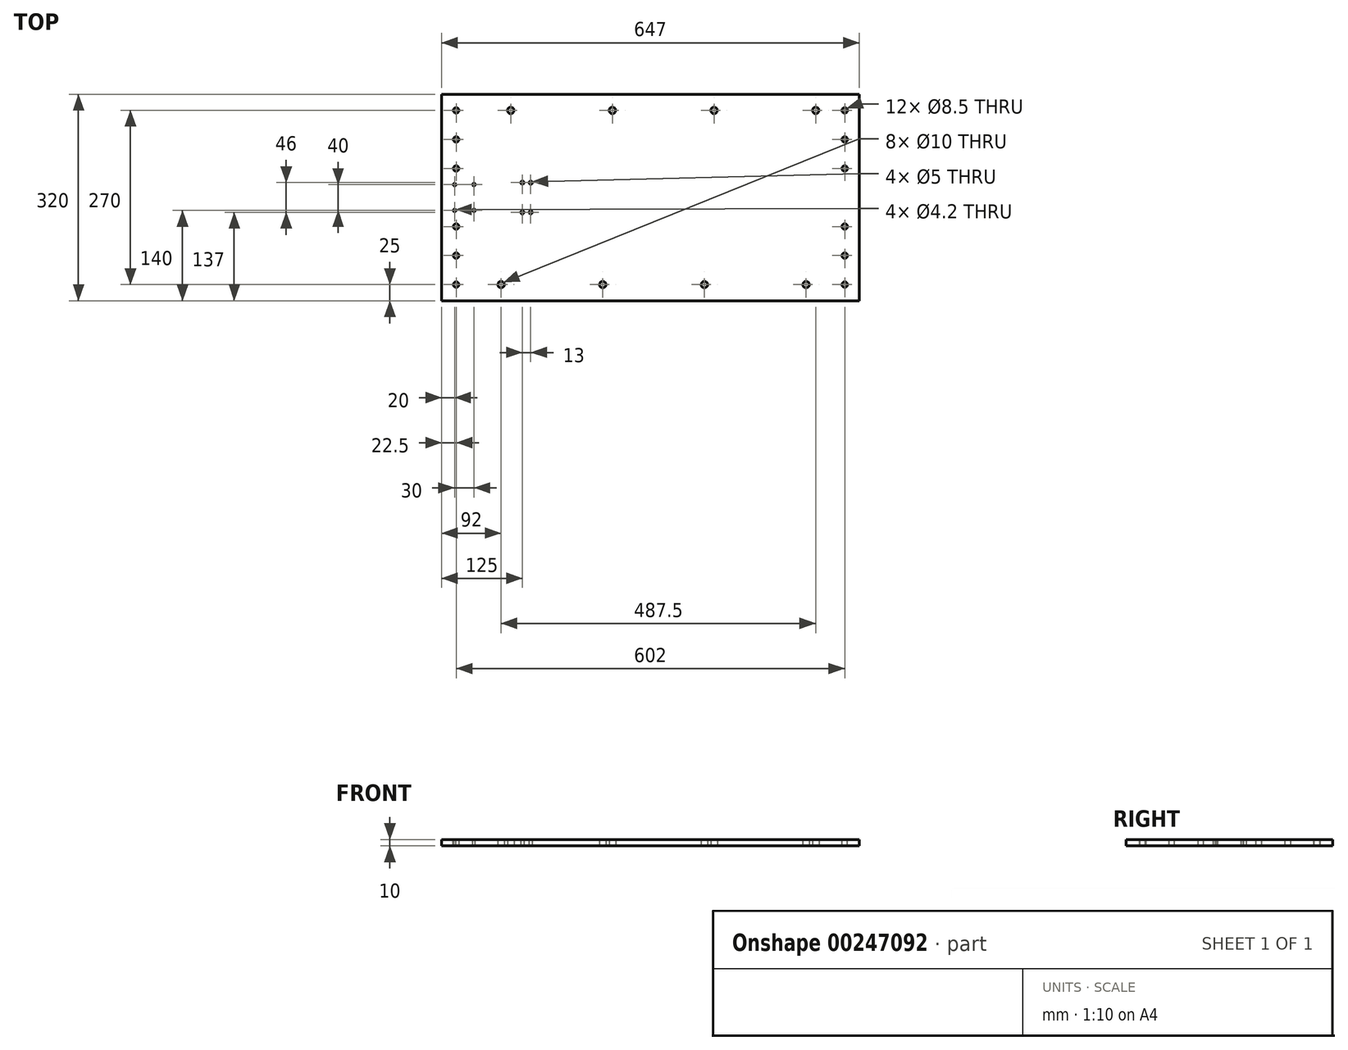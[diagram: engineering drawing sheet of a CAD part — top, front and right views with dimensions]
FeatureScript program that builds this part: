
annotation { "Feature Type Name" : "Feature", "Feature Type Description" : "" }
export const myFeature = defineFeature(function(context is Context, id is Id, definition is map)
    precondition{}
    {
        {
            var Q0;
            Q0=qCreatedBy(makeId("Top.planeOp"),FACE);
            var sketch = newSketch(context, id + "F0", { "sketchPlane" : qUnion([Q0])});
            skLineSegment(sketch, "E0.bottom", {"start": v(0, 0) * mm, "end": v(647, 0) * mm});
            skLineSegment(sketch, "E0.top", {"start": v(0, 320) * mm, "end": v(647, 320) * mm});
            skLineSegment(sketch, "E0.left", {"start": v(0, 0) * mm, "end": v(0, 320) * mm});
            skLineSegment(sketch, "E0.right", {"start": v(647, 0) * mm, "end": v(647, 320) * mm});
            skLineSegment(sketch, "E1", {"start": v(-62.37, 160) * mm, "end": v(1061.73, 160) * mm, "construction": true});
            skPoint(sketch, "E1.startSnap0", {"position": v(0, 160) * mm});
            skPoint(sketch, "E2", {"position": v(92, 25) * mm});
            skPoint(sketch, "E3.1.0.0", {"position": v(144.5, 25) * mm});
            skPoint(sketch, "E3.2.0.0", {"position": v(197, 25) * mm});
            skPoint(sketch, "E3.3.0.0", {"position": v(249.5, 25) * mm});
            skPoint(sketch, "E3.4.0.0", {"position": v(302, 25) * mm});
            skPoint(sketch, "E3.5.0.0", {"position": v(354.5, 25) * mm});
            skPoint(sketch, "E3.6.0.0", {"position": v(407, 25) * mm});
            skPoint(sketch, "E3.7.0.0", {"position": v(459.5, 25) * mm});
            skPoint(sketch, "E3.8.0.0", {"position": v(512, 25) * mm});
            skLineSegment(sketch, "E3.direction1", {"start": v(92, 25) * mm, "end": v(144.5, 25) * mm, "construction": true});
            skPoint(sketch, "E4", {"position": v(107, 295) * mm});
            skPoint(sketch, "E5.1.0.0", {"position": v(159.5, 295) * mm});
            skPoint(sketch, "E5.2.0.0", {"position": v(212, 295) * mm});
            skPoint(sketch, "E5.3.0.0", {"position": v(264.5, 295) * mm});
            skPoint(sketch, "E5.4.0.0", {"position": v(317, 295) * mm});
            skPoint(sketch, "E5.5.0.0", {"position": v(369.5, 295) * mm});
            skPoint(sketch, "E5.6.0.0", {"position": v(422, 295) * mm});
            skPoint(sketch, "E5.7.0.0", {"position": v(474.5, 295) * mm});
            skLineSegment(sketch, "E5.direction1", {"start": v(107, 295) * mm, "end": v(159.5, 295) * mm, "construction": true});
            skPoint(sketch, "E6.0.8.0", {"position": v(527, 295) * mm});
            skPoint(sketch, "E7.0.9.0", {"position": v(579.5, 295) * mm});
            skPoint(sketch, "E8.0.9.0", {"position": v(564.5, 25) * mm});
            skPoint(sketch, "E9", {"position": v(125, 183) * mm});
            skPoint(sketch, "E10.0.1.0", {"position": v(125, 137) * mm});
            skPoint(sketch, "E10.1.0.0", {"position": v(138, 183) * mm});
            skPoint(sketch, "E10.1.1.0", {"position": v(138, 137) * mm});
            skLineSegment(sketch, "E10.direction1", {"start": v(125, 183) * mm, "end": v(138, 183) * mm, "construction": true});
            skLineSegment(sketch, "E10.direction2", {"start": v(125, 183) * mm, "end": v(125, 137) * mm, "construction": true});
            skLineSegment(sketch, "E11", {"start": v(22.5, 340.04) * mm, "end": v(22.5, -24.03) * mm, "construction": true});
            skPoint(sketch, "E12", {"position": v(22.5, 160) * mm});
            skPoint(sketch, "E13.0.1.0", {"position": v(22.5, 205) * mm});
            skPoint(sketch, "E13.0.2.0", {"position": v(22.5, 250) * mm});
            skLineSegment(sketch, "E13.direction1", {"start": v(22.5, 160) * mm, "end": v(47.5, 160) * mm, "construction": true});
            skLineSegment(sketch, "E13.direction2", {"start": v(22.5, 160) * mm, "end": v(22.5, 205) * mm, "construction": true});
            skPoint(sketch, "E14.0.1.0", {"position": v(22.5, 115) * mm});
            skPoint(sketch, "E14.0.2.0", {"position": v(22.5, 70) * mm});
            skLineSegment(sketch, "E14.direction2", {"start": v(22.5, 160) * mm, "end": v(22.5, 115) * mm, "construction": true});
            skPoint(sketch, "E15.0.0.3", {"position": v(22.5, 25) * mm});
            skPoint(sketch, "E16.0.0.3", {"position": v(22.5, 295) * mm});
            skSolve(sketch);
        }
        {
            var Q0;
            Q0=makeQuery(id+"F0.imprint","IMPRINT",FACE,{"disambiguationData":[TD([[makeQuery(id+"F0.imprint","IMPRINT",EDGE,{"derivedFrom":sQuery(id+"F0.wireOp",EDGE,"E0.bottom")}),1.0]])]});
            extrude(context, id + "F1", {"entities" : qUnion([Q0]), "depth" : 10 * mm, "offsetDistance" : 25 * mm});
        }
        {
            var Q0;
            Q0=sQuery(id+"F0.wireOp",VERTEX,"E2");
            var Q1;
            Q1=sQuery(id+"F0.wireOp",VERTEX,"E3.3.0.0");
            var Q2;
            Q2=sQuery(id+"F0.wireOp",VERTEX,"E3.6.0.0");
            var Q3;
            Q3=sQuery(id+"F0.wireOp",VERTEX,"E8.0.9.0");
            var Q4;
            Q4=sQuery(id+"F0.wireOp",VERTEX,"E4");
            var Q5;
            Q5=sQuery(id+"F0.wireOp",VERTEX,"E5.3.0.0");
            var Q6;
            Q6=sQuery(id+"F0.wireOp",VERTEX,"E5.6.0.0");
            var Q7;
            Q7=sQuery(id+"F0.wireOp",VERTEX,"E7.0.9.0");
            var Q8;
            Q8=makeQuery(id+"F1.opExtrude","SWEPT_BODY",BODY,{"disambiguationData":[OSD([sQuery(id+"F0.wireOp",EDGE,"E0.bottom"),sQuery(id+"F0.wireOp",EDGE,"E0.top"),sQuery(id+"F0.wireOp",EDGE,"E0.left"),sQuery(id+"F0.wireOp",EDGE,"E0.right")])]});
            hole(context, id + "F2", {"style" : HoleStyle.SIMPLE, "endStyle" : HoleEndStyle.THROUGH, "oppositeDirection" : true, "holeDiameter" : 10 * mm, "majorDiameter" : 5 * mm, "isTappedThrough" : true, "tappedDepth" : 12 * mm, "tapClearance" : 3, "locations" : qUnion([Q0, Q1, Q2, Q3, Q4, Q5, Q6, Q7]), "scope" : qUnion([Q8])});
        }
        {
            var Q0;
            Q0=sQuery(id+"F0.wireOp",VERTEX,"E10.1.0.0");
            var Q1;
            Q1=sQuery(id+"F0.wireOp",VERTEX,"E9");
            var Q2;
            Q2=sQuery(id+"F0.wireOp",VERTEX,"E10.0.1.0");
            var Q3;
            Q3=sQuery(id+"F0.wireOp",VERTEX,"E10.1.1.0");
            var Q4;
            Q4=makeQuery(id+"F1.opExtrude","SWEPT_BODY",BODY,{"disambiguationData":[OSD([sQuery(id+"F0.wireOp",EDGE,"E0.bottom"),sQuery(id+"F0.wireOp",EDGE,"E0.top"),sQuery(id+"F0.wireOp",EDGE,"E0.left"),sQuery(id+"F0.wireOp",EDGE,"E0.right")])]});
            hole(context, id + "F3", {"style" : HoleStyle.SIMPLE, "endStyle" : HoleEndStyle.THROUGH, "oppositeDirection" : true, "holeDiameter" : 5 * mm, "majorDiameter" : 5 * mm, "isTappedThrough" : true, "tappedDepth" : 12 * mm, "tapClearance" : 3, "locations" : qUnion([Q0, Q1, Q2, Q3]), "scope" : qUnion([Q4])});
        }
        {
            var Q0;
            Q0=sQuery(id+"F0.wireOp",VERTEX,"E13.0.2.0");
            var Q1;
            Q1=sQuery(id+"F0.wireOp",VERTEX,"E13.0.1.0");
            var Q2;
            Q2=sQuery(id+"F0.wireOp",VERTEX,"E14.0.1.0");
            var Q3;
            Q3=sQuery(id+"F0.wireOp",VERTEX,"E14.0.2.0");
            var Q4;
            Q4=sQuery(id+"F0.wireOp",VERTEX,"E16.0.0.3");
            var Q5;
            Q5=sQuery(id+"F0.wireOp",VERTEX,"E15.0.0.3");
            var Q6;
            Q6=makeQuery(id+"F1.opExtrude","SWEPT_BODY",BODY,{"disambiguationData":[OSD([sQuery(id+"F0.wireOp",EDGE,"E0.bottom"),sQuery(id+"F0.wireOp",EDGE,"E0.top"),sQuery(id+"F0.wireOp",EDGE,"E0.left"),sQuery(id+"F0.wireOp",EDGE,"E0.right")])]});
            hole(context, id + "F4", {"style" : HoleStyle.SIMPLE, "endStyle" : HoleEndStyle.THROUGH, "oppositeDirection" : true, "holeDiameter" : 8.5 * mm, "majorDiameter" : 5 * mm, "isTappedThrough" : true, "tappedDepth" : 12 * mm, "tapClearance" : 3, "locations" : qUnion([Q0, Q1, Q2, Q3, Q4, Q5]), "scope" : qUnion([Q6])});
        }
        {
            var Q0;
            Q0=makeQuery(id+"F1.opExtrude","CAP_FACE",FACE,{"disambiguationData":[OSD([sQuery(id+"F0.wireOp",EDGE,"E0.bottom"),sQuery(id+"F0.wireOp",EDGE,"E0.top"),sQuery(id+"F0.wireOp",EDGE,"E0.left"),sQuery(id+"F0.wireOp",EDGE,"E0.right")])],"isStart":false});
            var sketch = newSketch(context, id + "F5", { "sketchPlane" : qUnion([Q0])});
            skPoint(sketch, "E17", {"position": v(20, 180) * mm});
            skPoint(sketch, "E18.0.1.0", {"position": v(20, 140) * mm});
            skPoint(sketch, "E18.1.0.0", {"position": v(50, 180) * mm});
            skPoint(sketch, "E18.1.1.0", {"position": v(50, 140) * mm});
            skLineSegment(sketch, "E18.direction1", {"start": v(20, 180) * mm, "end": v(50, 180) * mm, "construction": true});
            skLineSegment(sketch, "E18.direction2", {"start": v(20, 180) * mm, "end": v(20, 140) * mm, "construction": true});
            skSolve(sketch);
        }
        {
            var Q0;
            Q0=sQuery(id+"F5.wireOp",VERTEX,"E18.direction1.start");
            var Q1;
            Q1=sQuery(id+"F5.wireOp",VERTEX,"E18.1.0.0");
            var Q2;
            Q2=sQuery(id+"F5.wireOp",VERTEX,"E18.1.1.0");
            var Q3;
            Q3=sQuery(id+"F5.wireOp",VERTEX,"E18.0.1.0");
            var Q4;
            Q4=makeQuery(id+"F1.opExtrude","SWEPT_BODY",BODY,{"disambiguationData":[OSD([sQuery(id+"F0.wireOp",EDGE,"E0.bottom"),sQuery(id+"F0.wireOp",EDGE,"E0.top"),sQuery(id+"F0.wireOp",EDGE,"E0.left"),sQuery(id+"F0.wireOp",EDGE,"E0.right")])]});
            hole(context, id + "F6", {"style" : HoleStyle.SIMPLE, "endStyle" : HoleEndStyle.THROUGH, "holeDiameter" : 4.2 * mm, "majorDiameter" : 5 * mm, "isTappedThrough" : true, "tappedDepth" : 12 * mm, "tapClearance" : 3, "locations" : qUnion([Q0, Q1, Q2, Q3]), "scope" : qUnion([Q4])});
        }
        {
            var Q0;
            Q0=makeQuery(id+"F1.opExtrude","CAP_FACE",FACE,{"disambiguationData":[OSD([sQuery(id+"F0.wireOp",EDGE,"E0.bottom"),sQuery(id+"F0.wireOp",EDGE,"E0.top"),sQuery(id+"F0.wireOp",EDGE,"E0.left"),sQuery(id+"F0.wireOp",EDGE,"E0.right")])],"isStart":false});
            var Q1;
            Q1=makeQuery(id+"F1.opExtrude","CAP_FACE",FACE,{"disambiguationData":[OSD([sQuery(id+"F0.wireOp",EDGE,"E0.bottom"),sQuery(id+"F0.wireOp",EDGE,"E0.top"),sQuery(id+"F0.wireOp",EDGE,"E0.left"),sQuery(id+"F0.wireOp",EDGE,"E0.right")])],"isStart":false});
            var sketch = newSketch(context, id + "F7", { "sketchPlane" : qUnion([Q0, Q1])});
            skPoint(sketch, "E19", {"position": v(624.5, 160) * mm});
            skPoint(sketch, "E19.positionSnap0", {"position": v(647, 160) * mm});
            skPoint(sketch, "E20.0.1.0", {"position": v(624.5, 115) * mm});
            skPoint(sketch, "E20.0.2.0", {"position": v(624.5, 70) * mm});
            skPoint(sketch, "E20.0.3.0", {"position": v(624.5, 25) * mm});
            skLineSegment(sketch, "E20.direction1", {"start": v(624.5, 160) * mm, "end": v(649.5, 160) * mm, "construction": true});
            skLineSegment(sketch, "E20.direction2", {"start": v(624.5, 160) * mm, "end": v(624.5, 115) * mm, "construction": true});
            skPoint(sketch, "E21.0.1.0", {"position": v(624.5, 205) * mm});
            skPoint(sketch, "E21.0.2.0", {"position": v(624.5, 250) * mm});
            skPoint(sketch, "E21.0.3.0", {"position": v(624.5, 295) * mm});
            skLineSegment(sketch, "E21.direction2", {"start": v(624.5, 160) * mm, "end": v(624.5, 205) * mm, "construction": true});
            skSolve(sketch);
        }
        {
            var Q0;
            Q0=sQuery(id+"F7.wireOp",VERTEX,"E21.0.3.0");
            var Q1;
            Q1=sQuery(id+"F7.wireOp",VERTEX,"E21.0.2.0");
            var Q2;
            Q2=sQuery(id+"F7.wireOp",VERTEX,"E21.0.1.0");
            var Q3;
            Q3=sQuery(id+"F7.wireOp",VERTEX,"E20.0.1.0");
            var Q4;
            Q4=sQuery(id+"F7.wireOp",VERTEX,"E20.0.2.0");
            var Q5;
            Q5=sQuery(id+"F7.wireOp",VERTEX,"E20.0.3.0");
            var Q6;
            Q6=makeQuery(id+"F1.opExtrude","SWEPT_BODY",BODY,{"disambiguationData":[OSD([sQuery(id+"F0.wireOp",EDGE,"E0.bottom"),sQuery(id+"F0.wireOp",EDGE,"E0.top"),sQuery(id+"F0.wireOp",EDGE,"E0.left"),sQuery(id+"F0.wireOp",EDGE,"E0.right")])]});
            hole(context, id + "F8", {"style" : HoleStyle.SIMPLE, "endStyle" : HoleEndStyle.THROUGH, "holeDiameter" : 8.5 * mm, "majorDiameter" : 5 * mm, "isTappedThrough" : true, "tappedDepth" : 12 * mm, "tapClearance" : 3, "locations" : qUnion([Q0, Q1, Q2, Q3, Q4, Q5]), "scope" : qUnion([Q6])});
        }
    });
